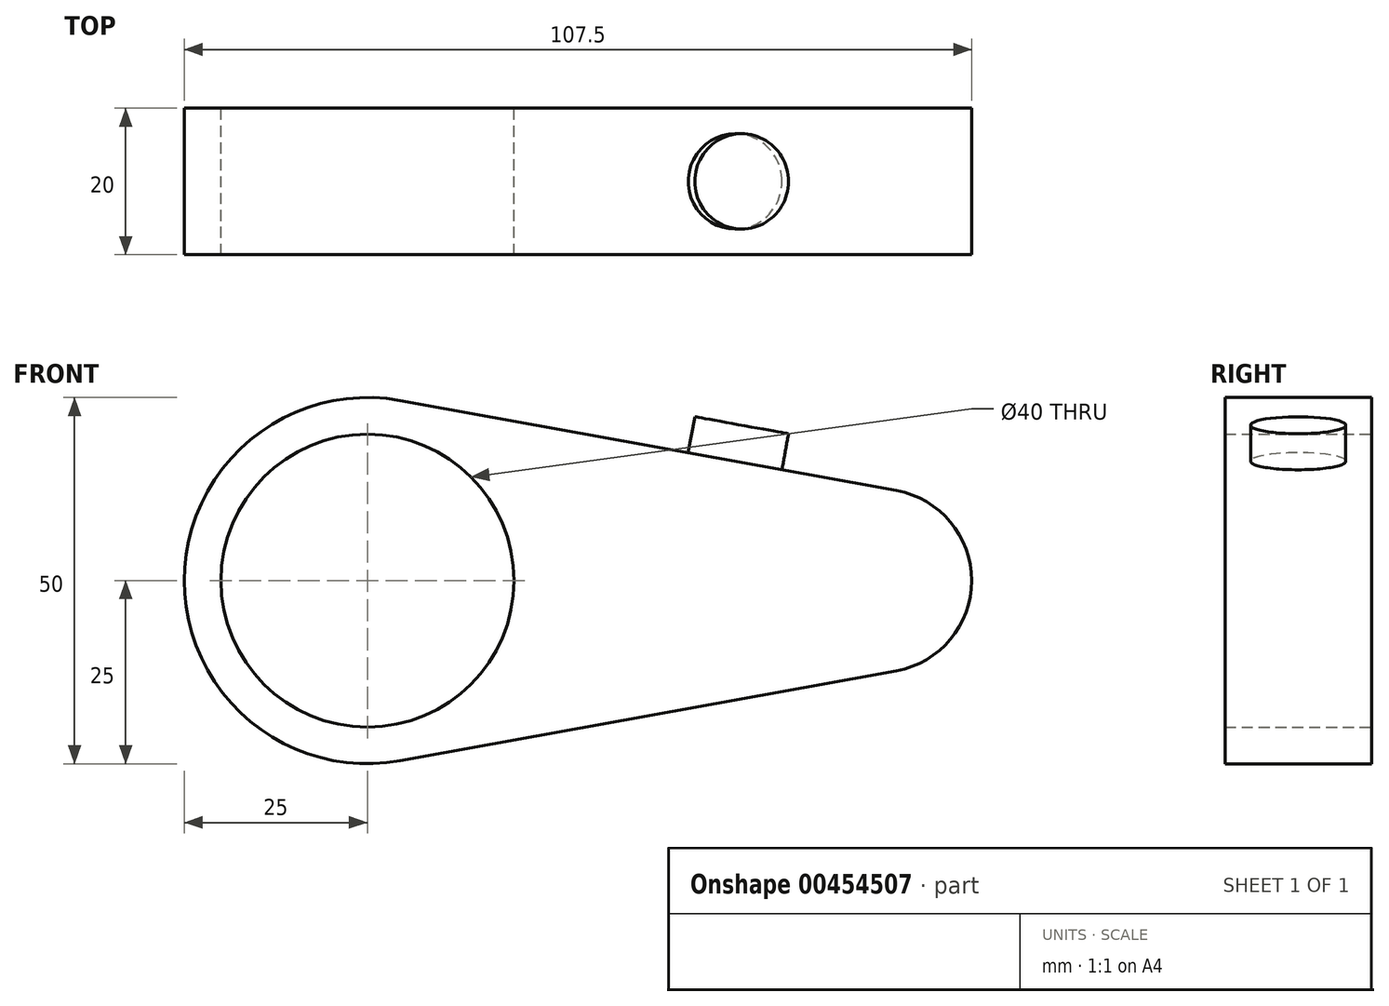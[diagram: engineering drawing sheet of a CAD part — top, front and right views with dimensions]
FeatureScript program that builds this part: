
annotation { "Feature Type Name" : "Feature", "Feature Type Description" : "" }
export const myFeature = defineFeature(function(context is Context, id is Id, definition is map)
    precondition{}
    {
        {
            var Q0;
            Q0=qCreatedBy(makeId("Front.planeOp"),FACE);
            var sketch = newSketch(context, id + "F0", { "sketchPlane" : qUnion([Q0])});
            skCircle(sketch, "E0", {"center": v(0, 0) * mm, "radius": 25 * mm});
            skCircle(sketch, "E1", {"center": v(70, 0) * mm, "radius": 12.5 * mm});
            skLineSegment(sketch, "E2", {"start": v(4.46, 24.6) * mm, "end": v(72.23, 12.3) * mm});
            skLineSegment(sketch, "E3", {"start": v(4.46, -24.6) * mm, "end": v(72.23, -12.3) * mm});
            skCircle(sketch, "E4", {"center": v(0, 0) * mm, "radius": 20 * mm});
            skSolve(sketch);
        }
        {
            var Q0;
            Q0 = qSketchRegion(id + "F0", true);
            extrude(context, id + "F1", {"entities" : qUnion([Q0]), "endBound" : BoundingType.SYMMETRIC, "depth" : 20 * mm});
        }
        {
            var Q0;
            Q0=makeQuery(id+"F1.opExtrude","SWEPT_FACE",FACE,{"disambiguationData":[OSD([sQuery(id+"F0.wireOp",EDGE,"E2")])]});
            var sketch = newSketch(context, id + "F2", { "sketchPlane" : qUnion([Q0])});
            skCircle(sketch, "E5", {"center": v(46.48, 0) * mm, "radius": 6.5 * mm});
            skPoint(sketch, "E5.centerSnap0", {"position": v(68.87, 0) * mm});
            skSolve(sketch);
        }
        {
            var Q0;
            Q0 = qSketchRegion(id + "F2", true);
            extrude(context, id + "F3", {"entities" : qUnion([Q0]), "operationType" : NewBodyOperationType.ADD, "depth" : 5 * mm});
        }
    });
